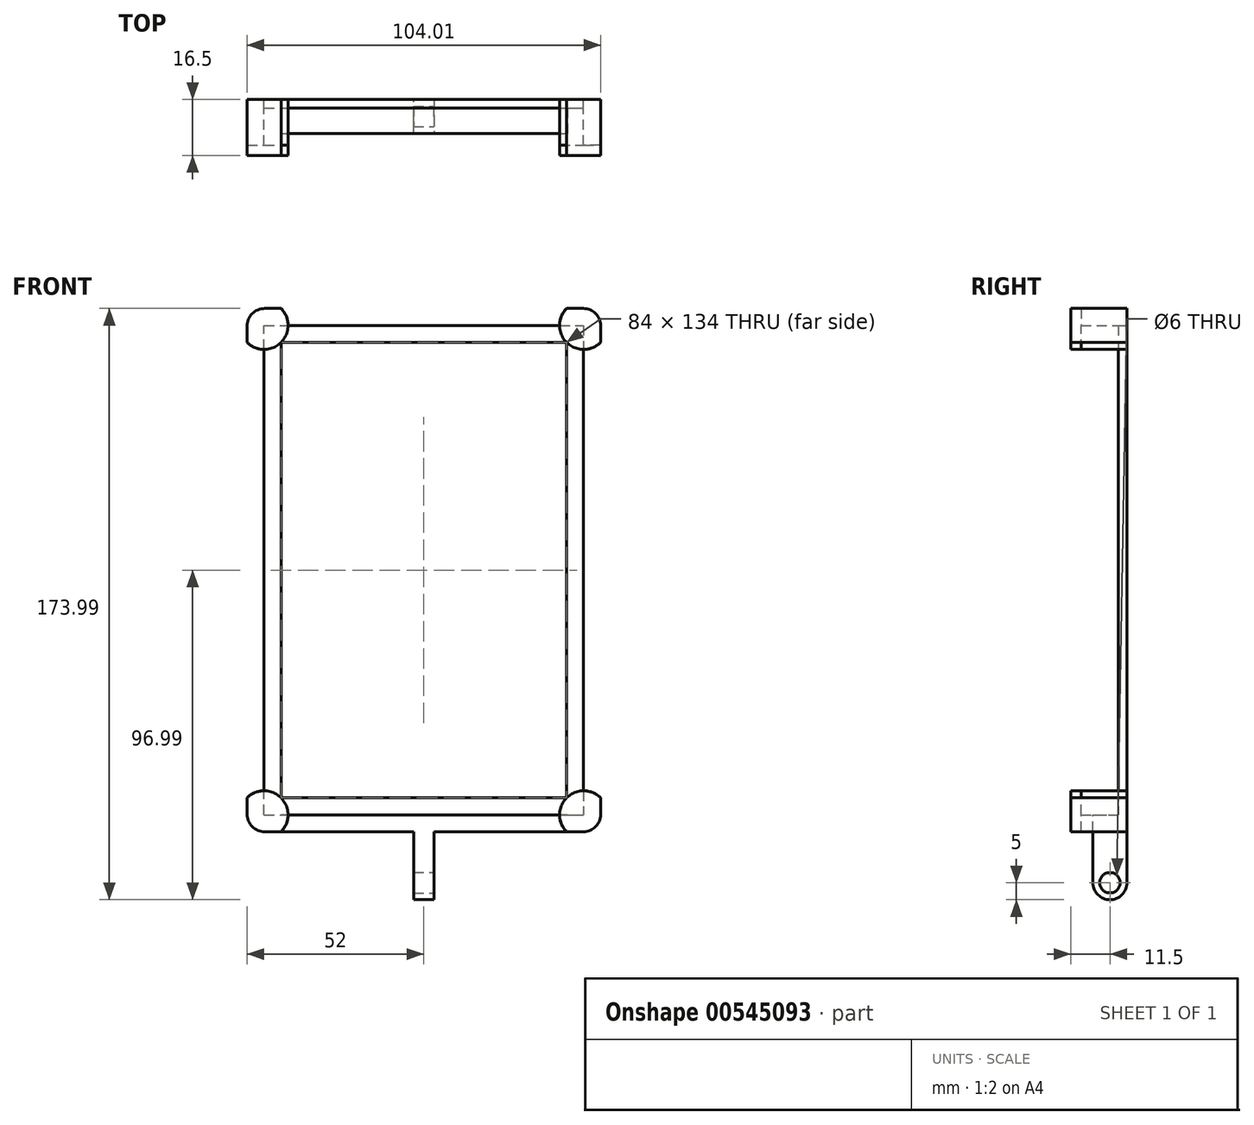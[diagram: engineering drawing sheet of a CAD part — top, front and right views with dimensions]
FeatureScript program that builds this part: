
annotation { "Feature Type Name" : "Feature", "Feature Type Description" : "" }
export const myFeature = defineFeature(function(context is Context, id is Id, definition is map)
    precondition{}
    {
        {
            var Q0;
            Q0=qCreatedBy(makeId("Front.planeOp"),FACE);
            var sketch = newSketch(context, id + "F0", { "sketchPlane" : qUnion([Q0])});
            skLineSegment(sketch, "E0", {"start": v(47, 0) * mm, "end": v(47, -72) * mm});
            skLineSegment(sketch, "E1", {"start": v(47, -72) * mm, "end": v(0, -72) * mm});
            skLineSegment(sketch, "E2.MirrorCS", {"start": v(47, 0) * mm, "end": v(47, 70) * mm});
            skLineSegment(sketch, "E3.MirrorCS", {"start": v(45, 72) * mm, "end": v(0, 72) * mm});
            skLineSegment(sketch, "E4.MirrorCS", {"start": v(-47, 0) * mm, "end": v(-47, 70) * mm});
            skLineSegment(sketch, "E5.MirrorCS", {"start": v(-45, 72) * mm, "end": v(0, 72) * mm});
            skLineSegment(sketch, "E6.MirrorCS", {"start": v(-47, 0) * mm, "end": v(-47, -72) * mm});
            skLineSegment(sketch, "E7.MirrorCS", {"start": v(-47, -72) * mm, "end": v(0, -72) * mm});
            skLineSegment(sketch, "E8", {"start": v(-47, 70) * mm, "end": v(-47, 72) * mm});
            skLineSegment(sketch, "E9", {"start": v(-47, 72) * mm, "end": v(-45, 72) * mm});
            skLineSegment(sketch, "E10", {"start": v(45, 72) * mm, "end": v(47, 72) * mm});
            skLineSegment(sketch, "E11", {"start": v(47, 72) * mm, "end": v(47, 70) * mm});
            skLineSegment(sketch, "E12.0", {"start": v(42, 0) * mm, "end": v(42, 67) * mm});
            skLineSegment(sketch, "E12.1", {"start": v(42, 0) * mm, "end": v(42, -67) * mm});
            skLineSegment(sketch, "E12.2", {"start": v(42, 67) * mm, "end": v(0, 67) * mm});
            skLineSegment(sketch, "E12.3", {"start": v(42, -67) * mm, "end": v(0, -67) * mm});
            skLineSegment(sketch, "E12.4", {"start": v(-42, 67) * mm, "end": v(0, 67) * mm});
            skLineSegment(sketch, "E12.5", {"start": v(-42, 0) * mm, "end": v(-42, 67) * mm});
            skLineSegment(sketch, "E12.6", {"start": v(-42, 0) * mm, "end": v(-42, -67) * mm});
            skLineSegment(sketch, "E12.7", {"start": v(-42, -67) * mm, "end": v(0, -67) * mm});
            skSolve(sketch);
        }
        {
            var Q0;
            Q0 = qSketchRegion(id + "F0", true);
            extrude(context, id + "F1", {"entities" : qUnion([Q0]), "depth" : 2.5 * mm, "offsetDistance" : 25 * mm});
        }
        {
            var Q0;
            Q0=makeQuery(id+"F1.opExtrude","CAP_FACE",FACE,{"disambiguationData":[OSD([sQuery(id+"F0.wireOp",EDGE,"E0"),sQuery(id+"F0.wireOp",EDGE,"E1"),sQuery(id+"F0.wireOp",EDGE,"E2.MirrorCS"),sQuery(id+"F0.wireOp",EDGE,"E3.MirrorCS"),sQuery(id+"F0.wireOp",EDGE,"E4.MirrorCS"),sQuery(id+"F0.wireOp",EDGE,"E5.MirrorCS"),sQuery(id+"F0.wireOp",EDGE,"E6.MirrorCS"),sQuery(id+"F0.wireOp",EDGE,"E7.MirrorCS"),sQuery(id+"F0.wireOp",EDGE,"E8"),sQuery(id+"F0.wireOp",EDGE,"E9"),sQuery(id+"F0.wireOp",EDGE,"E10"),sQuery(id+"F0.wireOp",EDGE,"E11"),sQuery(id+"F0.wireOp",EDGE,"E12.0"),sQuery(id+"F0.wireOp",EDGE,"E12.1"),sQuery(id+"F0.wireOp",EDGE,"E12.2"),sQuery(id+"F0.wireOp",EDGE,"E12.3"),sQuery(id+"F0.wireOp",EDGE,"E12.4"),sQuery(id+"F0.wireOp",EDGE,"E12.5"),sQuery(id+"F0.wireOp",EDGE,"E12.6"),sQuery(id+"F0.wireOp",EDGE,"E12.7")])],"isStart":false});
            var sketch = newSketch(context, id + "F2", { "sketchPlane" : qUnion([Q0])});
            skArc(sketch, "E13", {"start": v(-52, 67) * mm, "mid": v(-49.7, 65.47) * mm, "end": v(-47, 64.93) * mm});
            skArc(sketch, "E14", {"start": v(42, 77) * mm, "mid": v(40.47, 74.7) * mm, "end": v(39.93, 72) * mm});
            skArc(sketch, "E15", {"start": v(-42, -77) * mm, "mid": v(-40.47, -74.7) * mm, "end": v(-39.93, -72) * mm});
            skArc(sketch, "E16", {"start": v(52, -67) * mm, "mid": v(49.7, -65.47) * mm, "end": v(47, -64.93) * mm});
            skLineSegment(sketch, "E17.0", {"start": v(-52, -67) * mm, "end": v(-52, -77) * mm});
            skLineSegment(sketch, "E17.1", {"start": v(52, 77) * mm, "end": v(52, 70) * mm});
            skLineSegment(sketch, "E17.2", {"start": v(52, 67) * mm, "end": v(52, 70) * mm});
            skLineSegment(sketch, "E17.3", {"start": v(52, -67) * mm, "end": v(52, -77) * mm});
            skLineSegment(sketch, "E17.4", {"start": v(52, -77) * mm, "end": v(42, -77) * mm});
            skLineSegment(sketch, "E17.5", {"start": v(45, 77) * mm, "end": v(52, 77) * mm});
            skLineSegment(sketch, "E17.6", {"start": v(-52, -77) * mm, "end": v(-42, -77) * mm});
            skLineSegment(sketch, "E17.7", {"start": v(45, 77) * mm, "end": v(42, 77) * mm});
            skLineSegment(sketch, "E17.8", {"start": v(-45, 77) * mm, "end": v(-42, 77) * mm});
            skLineSegment(sketch, "E17.9", {"start": v(-52, 77) * mm, "end": v(-45, 77) * mm});
            skLineSegment(sketch, "E17.10", {"start": v(-52, 70) * mm, "end": v(-52, 77) * mm});
            skLineSegment(sketch, "E17.11", {"start": v(-52, 67) * mm, "end": v(-52, 70) * mm});
            skLineSegment(sketch, "E18", {"start": v(-47, 72) * mm, "end": v(-47, 64.93) * mm});
            skLineSegment(sketch, "E19", {"start": v(-47, 72) * mm, "end": v(-39.93, 72) * mm});
            skArc(sketch, "E20.trimOffspring", {"start": v(-39.93, 72) * mm, "mid": v(-40.47, 74.7) * mm, "end": v(-42, 77) * mm});
            skLineSegment(sketch, "E21", {"start": v(47, 72) * mm, "end": v(39.93, 72) * mm});
            skLineSegment(sketch, "E22", {"start": v(47, 72) * mm, "end": v(47, 64.93) * mm});
            skArc(sketch, "E23.trimOffspring", {"start": v(47, 64.93) * mm, "mid": v(49.7, 65.47) * mm, "end": v(52, 67) * mm});
            skLineSegment(sketch, "E24", {"start": v(-47, -72) * mm, "end": v(-47, -64.93) * mm});
            skLineSegment(sketch, "E25", {"start": v(-47, -72) * mm, "end": v(-39.93, -72) * mm});
            skArc(sketch, "E26.trimOffspring", {"start": v(-47, -64.93) * mm, "mid": v(-49.7, -65.47) * mm, "end": v(-52, -67) * mm});
            skLineSegment(sketch, "E27", {"start": v(47, -72) * mm, "end": v(39.93, -72) * mm});
            skLineSegment(sketch, "E28", {"start": v(47, -72) * mm, "end": v(47, -64.93) * mm});
            skArc(sketch, "E29.trimOffspring", {"start": v(39.93, -72) * mm, "mid": v(40.47, -74.7) * mm, "end": v(42, -77) * mm});
            skSolve(sketch);
        }
        {
            var Q0;
            Q0=makeQuery(id+"F2.imprint","IMPRINT",FACE,{"disambiguationData":[TD([[makeQuery(id+"F2.imprint","IMPRINT",EDGE,{"derivedFrom":sQuery(id+"F2.wireOp",EDGE,"E13")}),1.0]])]});
            var Q1;
            Q1=makeQuery(id+"F2.imprint","IMPRINT",FACE,{"disambiguationData":[TD([[makeQuery(id+"F2.imprint","IMPRINT",EDGE,{"derivedFrom":sQuery(id+"F2.wireOp",EDGE,"E14")}),1.0]])]});
            var Q2;
            Q2=makeQuery(id+"F2.imprint","IMPRINT",FACE,{"disambiguationData":[TD([[makeQuery(id+"F2.imprint","IMPRINT",EDGE,{"derivedFrom":sQuery(id+"F2.wireOp",EDGE,"E15")}),1.0]])]});
            var Q3;
            Q3=makeQuery(id+"F2.imprint","IMPRINT",FACE,{"disambiguationData":[TD([[makeQuery(id+"F2.imprint","IMPRINT",EDGE,{"derivedFrom":sQuery(id+"F2.wireOp",EDGE,"E16")}),1.0]])]});
            extrude(context, id + "F3", {"entities" : qUnion([Q0, Q1, Q2, Q3]), "operationType" : NewBodyOperationType.ADD, "endBound" : BoundingType.SYMMETRIC, "depth" : 22 * mm, "offsetDistance" : 25 * mm});
        }
        {
            var Q0;
            Q0=qCreatedBy(makeId("Top.planeOp"),FACE);
            var sketch = newSketch(context, id + "F4", { "sketchPlane" : qUnion([Q0])});
            skLineSegment(sketch, "E30", {"start": v(-75.06, 0) * mm, "end": v(76.42, 0) * mm});
            skLineSegment(sketch, "E31", {"start": v(76.42, 0) * mm, "end": v(76.42, 30.45) * mm});
            skLineSegment(sketch, "E32", {"start": v(76.42, 30.45) * mm, "end": v(-76.62, 30.45) * mm});
            skLineSegment(sketch, "E33", {"start": v(-76.62, 30.45) * mm, "end": v(-75.06, 0) * mm});
            skSolve(sketch);
        }
        {
            var Q0;
            Q0=makeQuery(id+"F4.imprint","IMPRINT",FACE,{"disambiguationData":[TD([[makeQuery(id+"F4.imprint","IMPRINT",EDGE,{"derivedFrom":sQuery(id+"F4.wireOp",EDGE,"E30")}),1.0]])]});
            extrude(context, id + "F5", {"entities" : qUnion([Q0]), "operationType" : NewBodyOperationType.REMOVE, "endBound" : BoundingType.SYMMETRIC, "depth" : 200 * mm, "offsetDistance" : 25 * mm});
        }
        {
            var Q0;
            Q0=makeQuery(id+"F3.opExtrude","SWEPT_EDGE",EDGE,{"disambiguationData":[OSD([sQuery(id+"F2.wireOp",EDGE,"E17.1"),sQuery(id+"F2.wireOp",EDGE,"E17.5")])]});
            var Q1;
            Q1=makeQuery(id+"F3.opExtrude","SWEPT_EDGE",EDGE,{"disambiguationData":[OSD([sQuery(id+"F2.wireOp",EDGE,"E17.3"),sQuery(id+"F2.wireOp",EDGE,"E17.4")])]});
            var Q2;
            Q2=makeQuery(id+"F3.opExtrude","SWEPT_EDGE",EDGE,{"disambiguationData":[OSD([sQuery(id+"F2.wireOp",EDGE,"E17.0"),sQuery(id+"F2.wireOp",EDGE,"E17.6")])]});
            var Q3;
            Q3=makeQuery(id+"F3.opExtrude","SWEPT_EDGE",EDGE,{"disambiguationData":[OSD([sQuery(id+"F2.wireOp",EDGE,"E17.9"),sQuery(id+"F2.wireOp",EDGE,"E17.10")])]});
            fillet(context, id + "F6", {"entities" : qUnion([Q0, Q1, Q2, Q3]), "radius" : 5 * mm, "tangentPropagation" : true, "allowEdgeOverflow" : false});
        }
        {
            var Q0;
            Q0=makeQuery(id+"F3.opExtrude","CAP_FACE",FACE,{"disambiguationData":[OSD([sQuery(id+"F2.wireOp",EDGE,"E13"),sQuery(id+"F2.wireOp",EDGE,"E17.8"),sQuery(id+"F2.wireOp",EDGE,"E17.9"),sQuery(id+"F2.wireOp",EDGE,"E17.10"),sQuery(id+"F2.wireOp",EDGE,"E17.11"),sQuery(id+"F2.wireOp",EDGE,"E18"),sQuery(id+"F2.wireOp",EDGE,"E19"),sQuery(id+"F2.wireOp",EDGE,"E20.trimOffspring")])],"isStart":false});
            var sketch = newSketch(context, id + "F7", { "sketchPlane" : qUnion([Q0])});
            skArc(sketch, "E34", {"start": v(-52, 67.02) * mm, "mid": v(-42, 67) * mm, "end": v(-42.02, 77) * mm});
            skLineSegment(sketch, "E35", {"start": v(-42, 77) * mm, "end": v(-51.98, 77) * mm});
            skLineSegment(sketch, "E36", {"start": v(-51.98, 77) * mm, "end": v(-52, 67) * mm});
            skArc(sketch, "E37.MirrorCS", {"start": v(52, 67.02) * mm, "mid": v(42, 67) * mm, "end": v(42.02, 77) * mm});
            skLineSegment(sketch, "E38.MirrorCS", {"start": v(42, 77) * mm, "end": v(51.98, 77) * mm});
            skLineSegment(sketch, "E39.MirrorCS", {"start": v(51.98, 77) * mm, "end": v(52, 67) * mm});
            skLineSegment(sketch, "E40.MirrorCS", {"start": v(-42, -77) * mm, "end": v(-51.98, -77) * mm});
            skLineSegment(sketch, "E41.MirrorCS", {"start": v(-51.98, -77) * mm, "end": v(-52, -67) * mm});
            skArc(sketch, "E42.MirrorCS", {"start": v(-52, -67.02) * mm, "mid": v(-42, -67) * mm, "end": v(-42.02, -77) * mm});
            skLineSegment(sketch, "E43.MirrorCS", {"start": v(42, -77) * mm, "end": v(51.98, -77) * mm});
            skLineSegment(sketch, "E44.MirrorCS", {"start": v(51.98, -77) * mm, "end": v(52, -67) * mm});
            skArc(sketch, "E45.MirrorCS", {"start": v(52, -67.02) * mm, "mid": v(42, -67) * mm, "end": v(42.02, -77) * mm});
            skSolve(sketch);
        }
        {
            var Q0;
            Q0 = qSketchRegion(id + "F7", true);
            extrude(context, id + "F8", {"entities" : qUnion([Q0]), "operationType" : NewBodyOperationType.ADD, "depth" : 3 * mm, "offsetDistance" : 25 * mm});
        }
        {
            var Q0;
            Q0=makeQuery(id+"F8.opExtrude","SWEPT_EDGE",EDGE,{"disambiguationData":[OSD([sQuery(id+"F7.wireOp",EDGE,"E43.MirrorCS"),sQuery(id+"F7.wireOp",EDGE,"E44.MirrorCS")])]});
            fillet(context, id + "F9", {"entities" : qUnion([Q0]), "radius" : 5.08 * mm, "tangentPropagation" : true, "allowEdgeOverflow" : false});
        }
        {
            var Q0;
            Q0=makeQuery(id+"F8.opExtrude","SWEPT_EDGE",EDGE,{"disambiguationData":[OSD([sQuery(id+"F7.wireOp",EDGE,"E40.MirrorCS"),sQuery(id+"F7.wireOp",EDGE,"E41.MirrorCS")])]});
            fillet(context, id + "F10", {"entities" : qUnion([Q0]), "radius" : 5.23 * mm, "tangentPropagation" : true, "allowEdgeOverflow" : false});
        }
        {
            var Q0;
            Q0=qCreatedBy(makeId("Front.planeOp"),FACE);
            var sketch = newSketch(context, id + "F11", { "sketchPlane" : qUnion([Q0])});
            skLineSegment(sketch, "E46", {"start": v(-42.09, -77) * mm, "end": v(42.21, -77) * mm});
            skLineSegment(sketch, "E47", {"start": v(42.21, -77) * mm, "end": v(42.21, -72) * mm});
            skLineSegment(sketch, "E48", {"start": v(42.21, -72) * mm, "end": v(-42.02, -72) * mm});
            skLineSegment(sketch, "E49", {"start": v(-42.02, -72) * mm, "end": v(-42.09, -77) * mm});
            skSolve(sketch);
        }
        {
            var Q0;
            Q0 = qSketchRegion(id + "F11", true);
            extrude(context, id + "F12", {"entities" : qUnion([Q0]), "operationType" : NewBodyOperationType.ADD, "depth" : 10 * mm, "offsetDistance" : 25 * mm});
        }
        {
            var Q0;
            Q0=makeQuery(id+"F8.opExtrude","SWEPT_EDGE",EDGE,{"disambiguationData":[OSD([sQuery(id+"F7.wireOp",EDGE,"E38.MirrorCS"),sQuery(id+"F7.wireOp",EDGE,"E39.MirrorCS")])]});
            fillet(context, id + "F13", {"entities" : qUnion([Q0]), "radius" : 5.08 * mm, "tangentPropagation" : true, "allowEdgeOverflow" : false});
        }
        {
            var Q0;
            Q0=makeQuery(id+"F8.opExtrude","SWEPT_EDGE",EDGE,{"disambiguationData":[OSD([sQuery(id+"F7.wireOp",EDGE,"E35"),sQuery(id+"F7.wireOp",EDGE,"E36")])]});
            fillet(context, id + "F14", {"entities" : qUnion([Q0]), "radius" : 5.2 * mm, "tangentPropagation" : true, "allowEdgeOverflow" : false});
        }
        {
            var Q0;
            Q0=makeQuery(id+"F12.opExtrude","SWEPT_FACE",FACE,{"disambiguationData":[OSD([sQuery(id+"F11.wireOp",EDGE,"E46")])]});
            var sketch = newSketch(context, id + "F15", { "sketchPlane" : qUnion([Q0])});
            skLineSegment(sketch, "E50", {"start": v(0, 0) * mm, "end": v(3, 0) * mm});
            skLineSegment(sketch, "E51", {"start": v(3, 0) * mm, "end": v(3, 10) * mm});
            skLineSegment(sketch, "E52", {"start": v(3, 10) * mm, "end": v(-3, 10) * mm});
            skLineSegment(sketch, "E53", {"start": v(-3, 10) * mm, "end": v(-3, 0) * mm});
            skLineSegment(sketch, "E54", {"start": v(-3, 0) * mm, "end": v(0, 0) * mm});
            skSolve(sketch);
        }
        {
            var Q0;
            Q0 = qSketchRegion(id + "F15", true);
            extrude(context, id + "F16", {"entities" : qUnion([Q0]), "operationType" : NewBodyOperationType.ADD, "depth" : 20 * mm, "offsetDistance" : 25 * mm});
        }
        {
            var Q0;
            Q0=makeQuery(id+"F16.opExtrude","SWEPT_FACE",FACE,{"disambiguationData":[OSD([sQuery(id+"F15.wireOp",EDGE,"E53")])]});
            var sketch = newSketch(context, id + "F17", { "sketchPlane" : qUnion([Q0])});
            skCircle(sketch, "E55", {"center": v(5, -92) * mm, "radius": 3 * mm});
            skPoint(sketch, "E56.trimOffspring.end.orphan", {"position": v(10, -92) * mm});
            skPoint(sketch, "E57.orphan", {"position": v(5, -97) * mm});
            skPoint(sketch, "E58.end.orphan", {"position": v(0, -92) * mm});
            skSolve(sketch);
        }
        {
            var Q0;
            Q0 = qSketchRegion(id + "F17", true);
            extrude(context, id + "F18", {"entities" : qUnion([Q0]), "operationType" : NewBodyOperationType.REMOVE, "endBound" : BoundingType.SYMMETRIC, "depth" : 25 * mm, "offsetDistance" : 25 * mm});
        }
        {
            var Q0;
            Q0=makeQuery(id+"F16.opExtrude","CAP_EDGE",EDGE,{"disambiguationData":[OSD([sQuery(id+"F15.wireOp",EDGE,"E52")])],"isStart":false});
            var Q1;
            Q1=makeQuery(id+"F16.opExtrude","CAP_EDGE",EDGE,{"disambiguationData":[OSD([sQuery(id+"F15.wireOp",EDGE,"E50"),sQuery(id+"F15.wireOp",EDGE,"E54")])],"isStart":false});
            fillet(context, id + "F19", {"entities" : qUnion([Q0, Q1]), "radius" : 5 * mm, "tangentPropagation" : true, "allowEdgeOverflow" : false});
        }
    });
